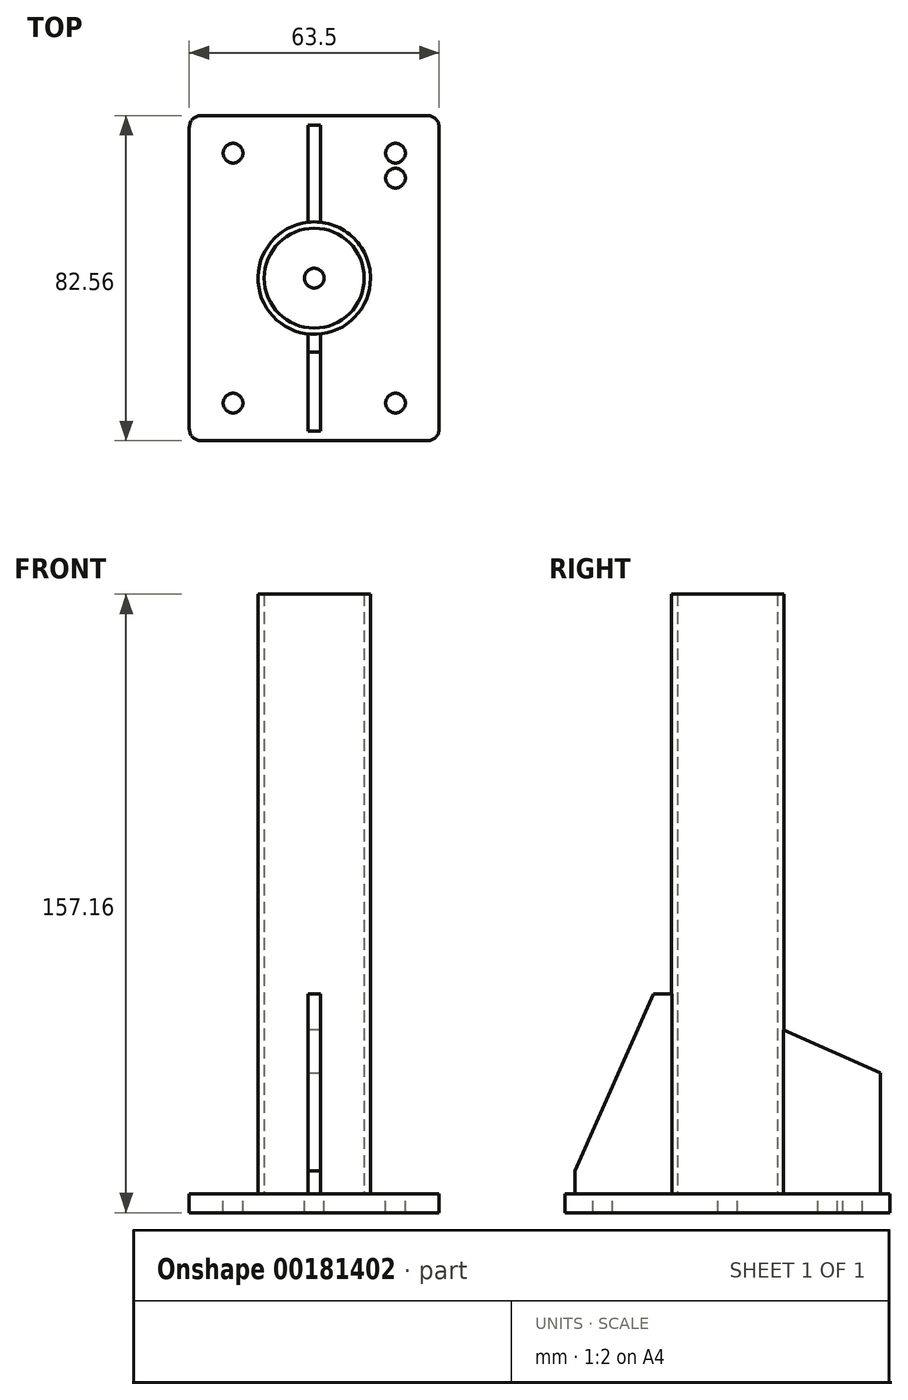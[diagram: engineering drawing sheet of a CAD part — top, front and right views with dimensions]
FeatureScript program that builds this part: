
annotation { "Feature Type Name" : "Feature", "Feature Type Description" : "" }
export const myFeature = defineFeature(function(context is Context, id is Id, definition is map)
    precondition{}
    {
        {
            var Q0;
            Q0=qCreatedBy(makeId("Top.planeOp"),FACE);
            var sketch = newSketch(context, id + "F0", { "sketchPlane" : qUnion([Q0])});
            skLineSegment(sketch, "E0.bottom", {"start": v(20.64, -31.75) * mm, "end": v(-20.64, -31.75) * mm, "construction": true});
            skLineSegment(sketch, "E0.top", {"start": v(20.64, 31.75) * mm, "end": v(-20.64, 31.75) * mm, "construction": true});
            skLineSegment(sketch, "E0.left", {"start": v(20.64, -31.75) * mm, "end": v(20.64, 31.75) * mm, "construction": true});
            skLineSegment(sketch, "E0.right", {"start": v(-20.64, -31.75) * mm, "end": v(-20.64, 31.75) * mm, "construction": true});
            skPoint(sketch, "E0.middle", {"position": v(0, 0) * mm});
            skLineSegment(sketch, "E1", {"start": v(-20.64, 25.4) * mm, "end": v(20.64, 25.4) * mm, "construction": true});
            skCircle(sketch, "E2", {"center": v(-20.64, 31.75) * mm, "radius": 2.5 * mm});
            skCircle(sketch, "E3", {"center": v(-20.64, 25.4) * mm, "radius": 2.5 * mm});
            skCircle(sketch, "E4", {"center": v(-20.64, -31.75) * mm, "radius": 2.5 * mm});
            skLineSegment(sketch, "E5", {"start": v(0, 31.75) * mm, "end": v(0, -31.75) * mm, "construction": true});
            skCircle(sketch, "E6.MirrorC", {"center": v(20.64, -31.75) * mm, "radius": 2.5 * mm});
            skCircle(sketch, "E7.MirrorC", {"center": v(20.64, 25.4) * mm, "radius": 2.5 * mm});
            skCircle(sketch, "E8.MirrorC", {"center": v(20.64, 31.75) * mm, "radius": 2.5 * mm});
            skLineSegment(sketch, "E9.bottom", {"start": v(31.75, -41.27) * mm, "end": v(-31.75, -41.28) * mm});
            skLineSegment(sketch, "E9.top", {"start": v(31.75, 41.28) * mm, "end": v(-31.75, 41.27) * mm});
            skLineSegment(sketch, "E9.left", {"start": v(31.75, -41.27) * mm, "end": v(31.75, 41.28) * mm});
            skLineSegment(sketch, "E9.right", {"start": v(-31.75, -41.28) * mm, "end": v(-31.75, 41.28) * mm});
            skCircle(sketch, "E10", {"center": v(0, 0) * mm, "radius": 14.29 * mm});
            skCircle(sketch, "E11", {"center": v(0, 0) * mm, "radius": 12.7 * mm});
            skLineSegment(sketch, "E12", {"start": v(-1.59, 31.75) * mm, "end": v(-1.59, 14.2) * mm});
            skLineSegment(sketch, "E13", {"start": v(-1.59, -14.2) * mm, "end": v(-1.59, -31.75) * mm});
            skLineSegment(sketch, "E14", {"start": v(0, 31.75) * mm, "end": v(-1.59, 31.75) * mm});
            skLineSegment(sketch, "E15", {"start": v(-1.59, -31.75) * mm, "end": v(0, -31.75) * mm});
            skLineSegment(sketch, "E16.MirrorCS", {"start": v(1.59, -14.2) * mm, "end": v(1.59, -31.75) * mm});
            skLineSegment(sketch, "E17.MirrorCS", {"start": v(1.59, -31.75) * mm, "end": v(0, -31.75) * mm});
            skLineSegment(sketch, "E18.MirrorCS", {"start": v(0, 31.75) * mm, "end": v(1.59, 31.75) * mm});
            skLineSegment(sketch, "E19.MirrorCS", {"start": v(1.59, 31.75) * mm, "end": v(1.59, 14.2) * mm});
            skCircle(sketch, "E20", {"center": v(0, 0) * mm, "radius": 2.5 * mm});
            skSolve(sketch);
        }
        {
            var Q0;
            Q0=makeQuery(id+"F0.imprint","IMPRINT",FACE,{"disambiguationData":[TD([[makeQuery(id+"F0.imprint","IMPRINT",EDGE,{"derivedFrom":sQuery(id+"F0.wireOp",EDGE,"E2")}),-1.0]])]});
            var Q1;
            {var subQ1=sQuery(id+"F0.wireOp",EDGE,"E13");Q1=makeQuery(id+"F0.imprint","IMPRINT",FACE,{"disambiguationData":[TD([[makeQuery(id+"F0.imprint","IMPRINT",EDGE,{"derivedFrom":subQ1}),1.0]])]});}
            var Q2;
            Q2=makeQuery(id+"F0.imprint","IMPRINT",FACE,{"disambiguationData":[TD([[makeQuery(id+"F0.imprint","IMPRINT",EDGE,{"derivedFrom":sQuery(id+"F0.wireOp",EDGE,"E11")}),-1.0]])]});
            var Q3;
            Q3=makeQuery(id+"F0.imprint","IMPRINT",FACE,{"disambiguationData":[TD([[makeQuery(id+"F0.imprint","IMPRINT",EDGE,{"derivedFrom":sQuery(id+"F0.wireOp",EDGE,"E11")}),1.0]])]});
            var Q4;
            {var subQ0=sQuery(id+"F0.wireOp",EDGE,"E12");Q4=makeQuery(id+"F0.imprint","IMPRINT",FACE,{"disambiguationData":[TD([[makeQuery(id+"F0.imprint","IMPRINT",EDGE,{"derivedFrom":subQ0}),1.0]])]});}
            var Q5;
            Q5=makeQuery(id+"F0.imprint","IMPRINT",FACE,{"disambiguationData":[TD([[makeQuery(id+"F0.imprint","IMPRINT",EDGE,{"derivedFrom":sQuery(id+"F0.wireOp",EDGE,"E3")}),1.0]])]});
            var Q6;
            Q6=makeQuery(id+"F0.imprint","IMPRINT",FACE,{"disambiguationData":[TD([[makeQuery(id+"F0.imprint","IMPRINT",EDGE,{"derivedFrom":sQuery(id+"F0.wireOp",EDGE,"E7.MirrorC")}),-1.0]])]});
            extrude(context, id + "F1", {"entities" : qUnion([Q0, Q1, Q2, Q3, Q4, Q5, Q6]), "oppositeDirection" : true, "depth" : 4.76 * mm, "offsetDistance" : 25 * mm});
        }
        {
            var Q0;
            Q0=makeQuery(id+"F0.imprint","IMPRINT",FACE,{"disambiguationData":[TD([[makeQuery(id+"F0.imprint","IMPRINT",EDGE,{"derivedFrom":sQuery(id+"F0.wireOp",EDGE,"E11")}),-1.0]])]});
            extrude(context, id + "F2", {"entities" : qUnion([Q0]), "operationType" : NewBodyOperationType.ADD, "depth" : 152.4 * mm, "offsetDistance" : 25 * mm});
        }
        {
            var Q0;
            {var subQ1=sQuery(id+"F0.wireOp",EDGE,"E13");Q0=makeQuery(id+"F0.imprint","IMPRINT",FACE,{"disambiguationData":[TD([[makeQuery(id+"F0.imprint","IMPRINT",EDGE,{"derivedFrom":subQ1}),1.0]])]});}
            var Q1;
            {var subQ0=sQuery(id+"F0.wireOp",EDGE,"E12");Q1=makeQuery(id+"F0.imprint","IMPRINT",FACE,{"disambiguationData":[TD([[makeQuery(id+"F0.imprint","IMPRINT",EDGE,{"derivedFrom":subQ0}),1.0]])]});}
            extrude(context, id + "F3", {"entities" : qUnion([Q0, Q1]), "operationType" : NewBodyOperationType.ADD, "depth" : 50.8 * mm, "offsetDistance" : 25 * mm});
        }
        {
            var Q0;
            Q0=makeQuery(id+"F3.opExtrude","SWEPT_FACE",FACE,{"disambiguationData":[OSD([sQuery(id+"F0.wireOp",EDGE,"E15"),sQuery(id+"F0.wireOp",EDGE,"E17.MirrorCS")])]});
            extrude(context, id + "F4", {"entities" : qUnion([Q0]), "operationType" : NewBodyOperationType.ADD, "depth" : 7.05 * mm, "offsetDistance" : 25 * mm});
        }
        {
            var Q0;
            Q0=makeQuery(id+"F3.opExtrude","SWEPT_FACE",FACE,{"disambiguationData":[OSD([sQuery(id+"F0.wireOp",EDGE,"E14"),sQuery(id+"F0.wireOp",EDGE,"E18.MirrorCS")])]});
            extrude(context, id + "F5", {"entities" : qUnion([Q0]), "operationType" : NewBodyOperationType.ADD, "depth" : 7.05 * mm, "offsetDistance" : 25 * mm});
        }
        {
            var Q0;
            Q0=makeQuery(id+"F1.opExtrude","SWEPT_EDGE",EDGE,{"disambiguationData":[OSD([sQuery(id+"F0.wireOp",EDGE,"E9.bottom"),sQuery(id+"F0.wireOp",EDGE,"E9.left")])]});
            var Q1;
            Q1=makeQuery(id+"F1.opExtrude","SWEPT_EDGE",EDGE,{"disambiguationData":[OSD([sQuery(id+"F0.wireOp",EDGE,"E9.top"),sQuery(id+"F0.wireOp",EDGE,"E9.left")])]});
            var Q2;
            Q2=makeQuery(id+"F1.opExtrude","SWEPT_EDGE",EDGE,{"disambiguationData":[OSD([sQuery(id+"F0.wireOp",EDGE,"E9.top"),sQuery(id+"F0.wireOp",EDGE,"E9.right")])]});
            var Q3;
            Q3=makeQuery(id+"F1.opExtrude","SWEPT_EDGE",EDGE,{"disambiguationData":[OSD([sQuery(id+"F0.wireOp",EDGE,"E9.bottom"),sQuery(id+"F0.wireOp",EDGE,"E9.right")])]});
            fillet(context, id + "F6", {"entities" : qUnion([Q0, Q1, Q2, Q3]), "radius" : 3 * mm, "tangentPropagation" : true, "allowEdgeOverflow" : false});
        }
        {
            var Q0;
            {var subQ0=sQuery(id+"F0.wireOp",EDGE,"E17.MirrorCS");var subQ1=sQuery(id+"F0.wireOp",EDGE,"E15");Q0=makeQuery(id+"F4.opExtrude","CAP_EDGE",EDGE,{"disambiguationData":[OSD([subQ1,subQ0]),TDD([makeQuery(id+"F3.opExtrude","CAP_EDGE",EDGE,{"disambiguationData":[OSD([subQ1,subQ0])],"isStart":false})])],"isStart":false});}
            chamfer(context, id + "F7", {"entities" : qUnion([Q0]), "chamferType" : ChamferType.TWO_OFFSETS, "width1" : 20 * mm, "oppositeDirection" : false, "width2" : 45 * mm, "tangentPropagation" : true});
        }
        {
            var Q0;
            {var subQ0=sQuery(id+"F0.wireOp",EDGE,"E18.MirrorCS");var subQ1=sQuery(id+"F0.wireOp",EDGE,"E14");Q0=makeQuery(id+"F5.opExtrude","CAP_EDGE",EDGE,{"disambiguationData":[OSD([subQ1,subQ0]),TDD([makeQuery(id+"F3.opExtrude","CAP_EDGE",EDGE,{"disambiguationData":[OSD([subQ1,subQ0])],"isStart":false})])],"isStart":false});}
            chamfer(context, id + "F8", {"entities" : qUnion([Q0]), "chamferType" : ChamferType.TWO_OFFSETS, "width1" : 45 * mm, "oppositeDirection" : false, "width2" : 20 * mm, "tangentPropagation" : true});
        }
    });
